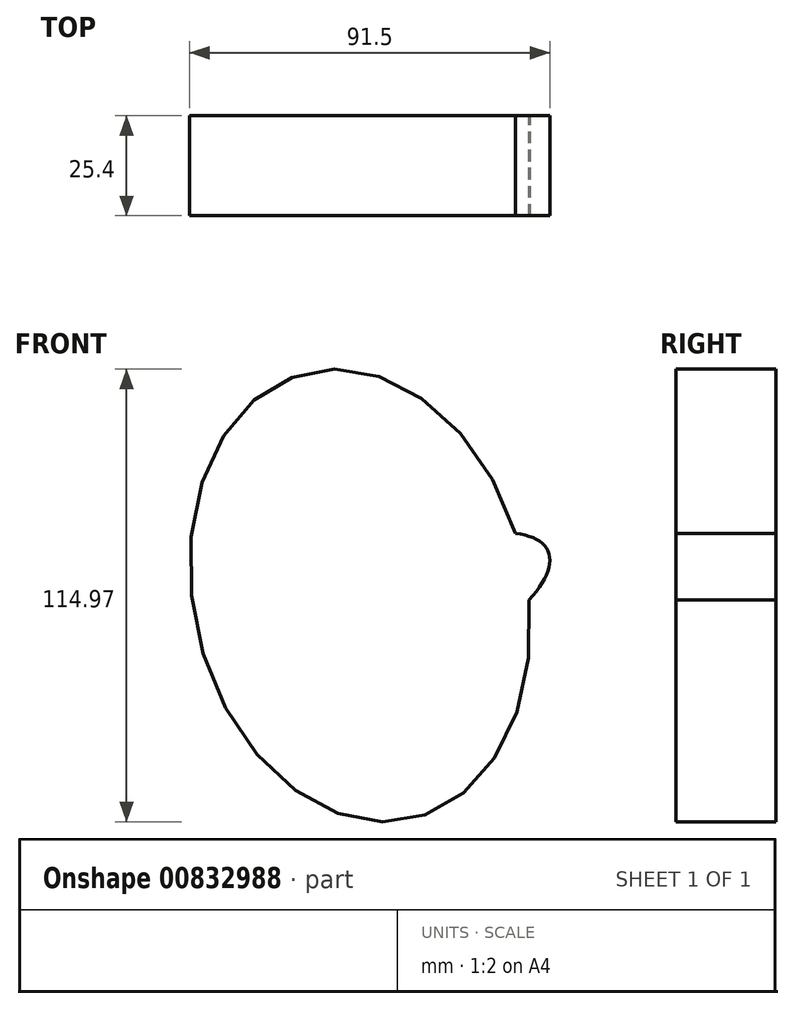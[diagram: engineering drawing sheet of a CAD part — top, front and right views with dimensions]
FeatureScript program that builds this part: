
annotation { "Feature Type Name" : "Feature", "Feature Type Description" : "" }
export const myFeature = defineFeature(function(context is Context, id is Id, definition is map)
    precondition{}
    {
        {
            var Q0;
            Q0=qCreatedBy(makeId("Front.planeOp"),FACE);
            var sketch = newSketch(context, id + "F0", { "sketchPlane" : qUnion([Q0])});
            skEllipse(sketch, "E0", {"center": v(-39.5, 39.48) * mm, "majorRadius": 58.2 * mm, "minorRadius": 42.32 * mm, "majorAxis": v(0.23, -0.97)});
            skEllipse(sketch, "E1", {"center": v(-22.34, 36.7) * mm, "majorRadius": 33.7 * mm, "minorRadius": 13.4 * mm, "majorAxis": v(0.9, 0.42)});
            skSolve(sketch);
        }
        {
            var Q0;
            Q0 = qSketchRegion(id + "F0", true);
            var Q1;
            {var subQ0=sQuery(id+"F0.wireOp",EDGE,"E1");var subQ1=sQuery(id+"F0.wireOp",EDGE,"E0");var subQ2=makeQuery(id+"F0.imprint","INTERSECT",VERTEX,{"disambiguationData":[OD(0.0)],"derivedFrom":[subQ1,subQ0]});Q1=makeQuery(id+"F0.imprint","IMPRINT",FACE,{"disambiguationData":[TD([[makeQuery(id+"F0.imprint","IMPRINT",EDGE,{"disambiguationData":[TD([[subQ2,1.0]])],"derivedFrom":subQ1}),1.0]])]});}
            extrude(context, id + "F1", {"entities" : qUnion([Q0, Q1]), "depth" : 25.4 * mm, "offsetDistance" : 25.4 * mm});
        }
    });
